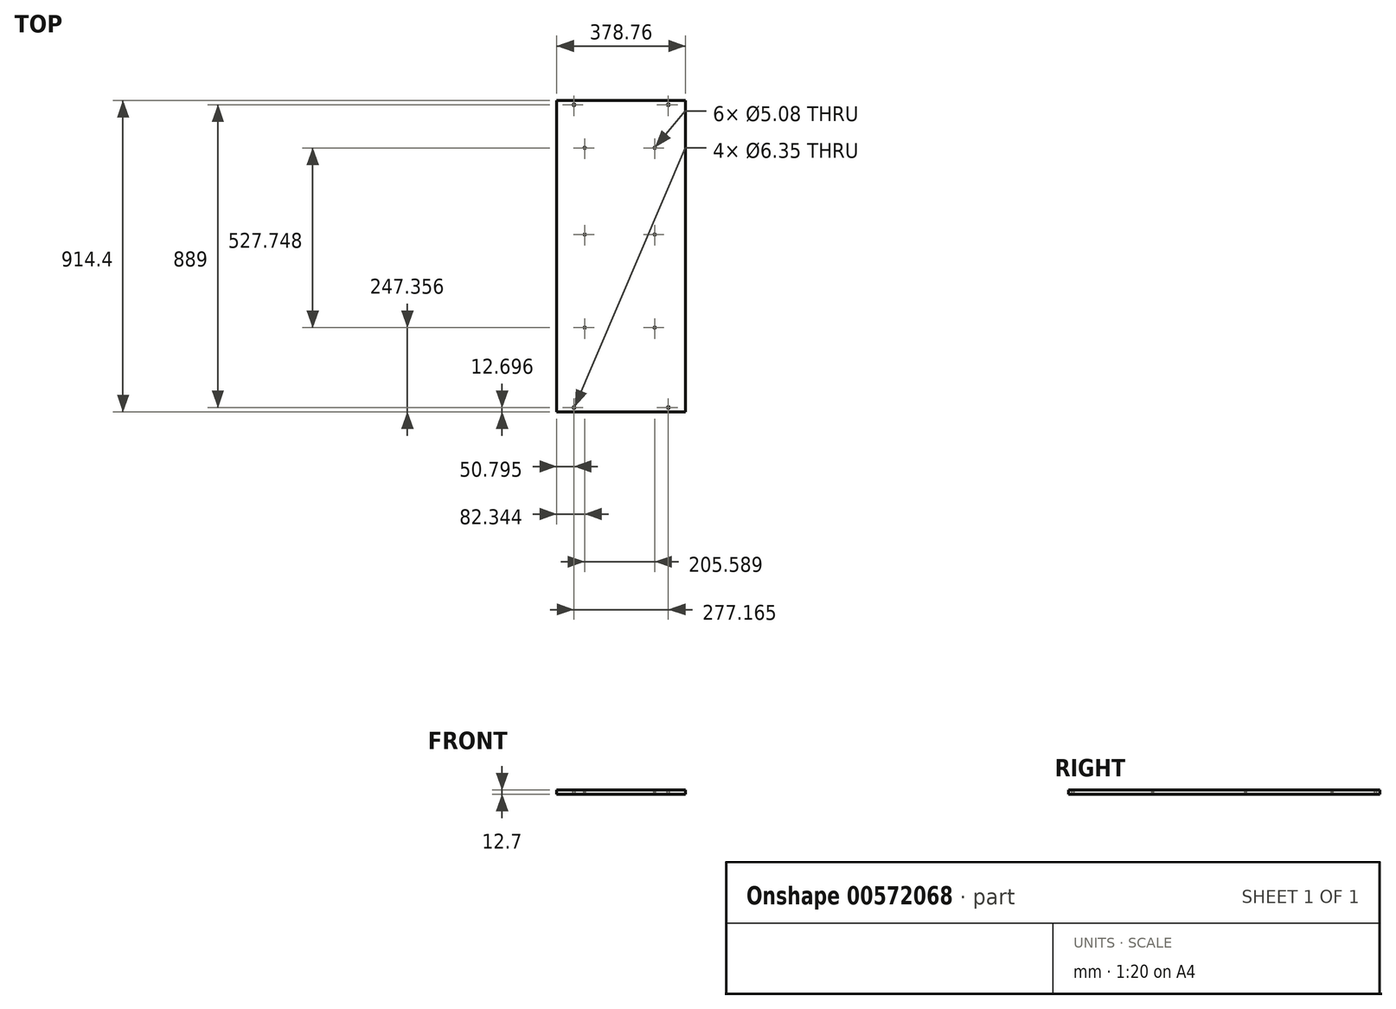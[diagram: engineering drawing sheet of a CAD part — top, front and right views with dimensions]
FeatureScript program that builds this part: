
annotation { "Feature Type Name" : "Feature", "Feature Type Description" : "" }
export const myFeature = defineFeature(function(context is Context, id is Id, definition is map)
    precondition{}
    {
        {
            var Q0;
            Q0=qCreatedBy(makeId("Top.planeOp"),FACE);
            var sketch = newSketch(context, id + "F0", { "sketchPlane" : qUnion([Q0])});
            skLineSegment(sketch, "E0.bottom", {"start": v(185.25, 527.23) * mm, "end": v(-193.51, 527.23) * mm});
            skLineSegment(sketch, "E0.top", {"start": v(185.25, -387.17) * mm, "end": v(-193.51, -387.17) * mm});
            skLineSegment(sketch, "E0.left", {"start": v(185.25, 527.23) * mm, "end": v(185.25, -387.17) * mm});
            skLineSegment(sketch, "E0.right", {"start": v(-193.51, 527.23) * mm, "end": v(-193.51, -387.17) * mm});
            skPoint(sketch, "E0.middle", {"position": v(-4.13, 70.03) * mm});
            skSolve(sketch);
        }
        {
            var Q0;
            Q0 = qSketchRegion(id + "F0", true);
            extrude(context, id + "F1", {"entities" : qUnion([Q0]), "depth" : 12.7 * mm, "offsetDistance" : 25.4 * mm});
        }
        {
            var Q0;
            Q0=makeQuery(id+"F1.opExtrude","CAP_FACE",FACE,{"disambiguationData":[OSD([sQuery(id+"F0.wireOp",EDGE,"E0.bottom"),sQuery(id+"F0.wireOp",EDGE,"E0.top"),sQuery(id+"F0.wireOp",EDGE,"E0.left"),sQuery(id+"F0.wireOp",EDGE,"E0.right")])],"isStart":false});
            var sketch = newSketch(context, id + "F2", { "sketchPlane" : qUnion([Q0])});
            skCircle(sketch, "E1", {"center": v(-142.71, 514.53) * mm, "radius": 3.18 * mm});
            skCircle(sketch, "E2", {"center": v(134.45, 514.53) * mm, "radius": 3.18 * mm});
            skCircle(sketch, "E3", {"center": v(-142.71, -374.47) * mm, "radius": 3.17 * mm});
            skCircle(sketch, "E4", {"center": v(134.45, -374.47) * mm, "radius": 3.17 * mm});
            skLineSegment(sketch, "E5", {"start": v(-142.71, 514.53) * mm, "end": v(-142.71, 517.7) * mm});
            skLineSegment(sketch, "E6", {"start": v(-142.71, 517.7) * mm, "end": v(-142.71, 527.23) * mm});
            skLineSegment(sketch, "E7", {"start": v(134.45, 514.53) * mm, "end": v(134.45, 517.7) * mm});
            skLineSegment(sketch, "E8", {"start": v(134.45, 517.7) * mm, "end": v(134.45, 527.23) * mm});
            skLineSegment(sketch, "E9", {"start": v(134.45, -374.47) * mm, "end": v(134.45, -377.65) * mm});
            skLineSegment(sketch, "E10", {"start": v(134.45, -377.65) * mm, "end": v(134.45, -387.17) * mm});
            skLineSegment(sketch, "E11", {"start": v(-142.71, -374.47) * mm, "end": v(-142.71, -377.65) * mm});
            skLineSegment(sketch, "E12", {"start": v(-142.71, -377.65) * mm, "end": v(-142.71, -387.17) * mm});
            skSolve(sketch);
        }
        {
            var Q0;
            Q0 = qSketchRegion(id + "F2", true);
            extrude(context, id + "F3", {"entities" : qUnion([Q0]), "operationType" : NewBodyOperationType.REMOVE, "endBound" : BoundingType.THROUGH_ALL, "oppositeDirection" : true, "depth" : 25.4 * mm, "offsetDistance" : 25.4 * mm});
        }
        {
            var Q0;
            Q0=makeQuery(id+"F1.opExtrude","CAP_FACE",FACE,{"disambiguationData":[OSD([sQuery(id+"F0.wireOp",EDGE,"E0.bottom"),sQuery(id+"F0.wireOp",EDGE,"E0.top"),sQuery(id+"F0.wireOp",EDGE,"E0.left"),sQuery(id+"F0.wireOp",EDGE,"E0.right")])],"isStart":false});
            var sketch = newSketch(context, id + "F4", { "sketchPlane" : qUnion([Q0])});
            skPoint(sketch, "E13", {"position": v(-111.17, 387.93) * mm});
            skPoint(sketch, "E14", {"position": v(94.42, 387.93) * mm});
            skPoint(sketch, "E15", {"position": v(94.42, 133.6) * mm});
            skPoint(sketch, "E16", {"position": v(94.42, -139.81) * mm});
            skPoint(sketch, "E17", {"position": v(-111.17, -139.81) * mm});
            skPoint(sketch, "E18", {"position": v(-111.17, 133.6) * mm});
            skSolve(sketch);
        }
        {
            var Q0;
            Q0=sQuery(id+"F4.wireOp",VERTEX,"E13");
            var Q1;
            Q1=sQuery(id+"F4.wireOp",VERTEX,"E14");
            var Q2;
            Q2=sQuery(id+"F4.wireOp",VERTEX,"E15");
            var Q3;
            Q3=sQuery(id+"F4.wireOp",VERTEX,"E18");
            var Q4;
            Q4=sQuery(id+"F4.wireOp",VERTEX,"E17");
            var Q5;
            Q5=sQuery(id+"F4.wireOp",VERTEX,"E16");
            var Q6;
            Q6=makeQuery(id+"F1.opExtrude","SWEPT_BODY",BODY,{"disambiguationData":[OSD([sQuery(id+"F0.wireOp",EDGE,"E0.bottom"),sQuery(id+"F0.wireOp",EDGE,"E0.top"),sQuery(id+"F0.wireOp",EDGE,"E0.left"),sQuery(id+"F0.wireOp",EDGE,"E0.right")])]});
            hole(context, id + "F5", {"style" : HoleStyle.SIMPLE, "endStyle" : HoleEndStyle.THROUGH, "holeDiameter" : 5.08 * mm, "majorDiameter" : 6.35 * mm, "isTappedThrough" : true, "tappedDepth" : 12.7 * mm, "tapClearance" : 3, "locations" : qUnion([Q0, Q1, Q2, Q3, Q4, Q5]), "scope" : qUnion([Q6])});
        }
    });
